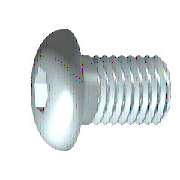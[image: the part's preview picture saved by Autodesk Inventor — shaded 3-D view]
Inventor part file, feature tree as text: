
AUTODESK INVENTOR PART (.ipt)
format: ipt  version: 2015 (Build 190159000, 159)  size: 196,096 bytes
history: native  units: mm (DEFAULTED — no unit token found)
features: sketch x2, extrude x1, plane x1, fillet x1
ambient origin geometry x7: Origin, YZ Plane, XY Plane, X Axis, Y Axis, Z Axis, Center Point
bodies: Solid1 (feature_tree), Body (feature_tree)
feature tree (5):
  extrude  "Slot"  Depth=1.8542mm
  plane  "Work Plane1"
  fillet  "Fillet2"  Radius=1.8542mm
  sketch  "Sketch1"  dims[d1=7.93476mm d2=1.59014mm d3=1.8542mm]
  sketch  "Sketch2"  dims[d4=1.1176mm d5=60.0deg d6=3.5052mm d7=3.5052mm d8=2.287693mm d9=6.6548mm d10=90.0deg d11=10.0mm d12=0.0mm d13=7.93476mm d14=0.0mm d15=0.486918mm d16=0.486918mm d17=1.6002mm d19=0.0mm d26=9.525mm d27=45.0deg d28=0.0mm d29=0.0mm d30=0.1mm]
